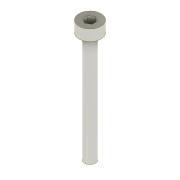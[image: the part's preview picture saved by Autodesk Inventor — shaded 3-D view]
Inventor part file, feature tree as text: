
AUTODESK INVENTOR PART (.ipt)
format: ipt  version: 2022 (Build 260153000, 153)  size: 92,672 bytes
history: native  units: mm
features: extrude x3, sketch x3
ambient origin geometry x8: Origin, YZ Plane, XZ Plane, XY Plane, X Axis, Y Axis, Z Axis, Center Point
bodies: Solid1 (feature_tree)
feature tree (6):
  extrude  "Extrusion1"  Depth=20.0mm TaperAngle=0.0deg
  extrude  "Extrusion2"  Depth=2.0mm TaperAngle=0.0deg
  extrude  "Extrusion3"  [1 undecoded]
  sketch  "Sketch1"  dims[d0=2.0mm d1=20.0mm d2=0.0mm]
  sketch  "Sketch2"  dims[d3=4.0mm d4=2.0mm d5=0.0mm]
  sketch  "Sketch3"  dims[d6=1.0mm d7=0.0mm]
note: 1 required parameter value undecoded (feature->parameter linkage not recoverable at this tier; creation-order binding heuristic only, values carry confidence <= 0.55)
